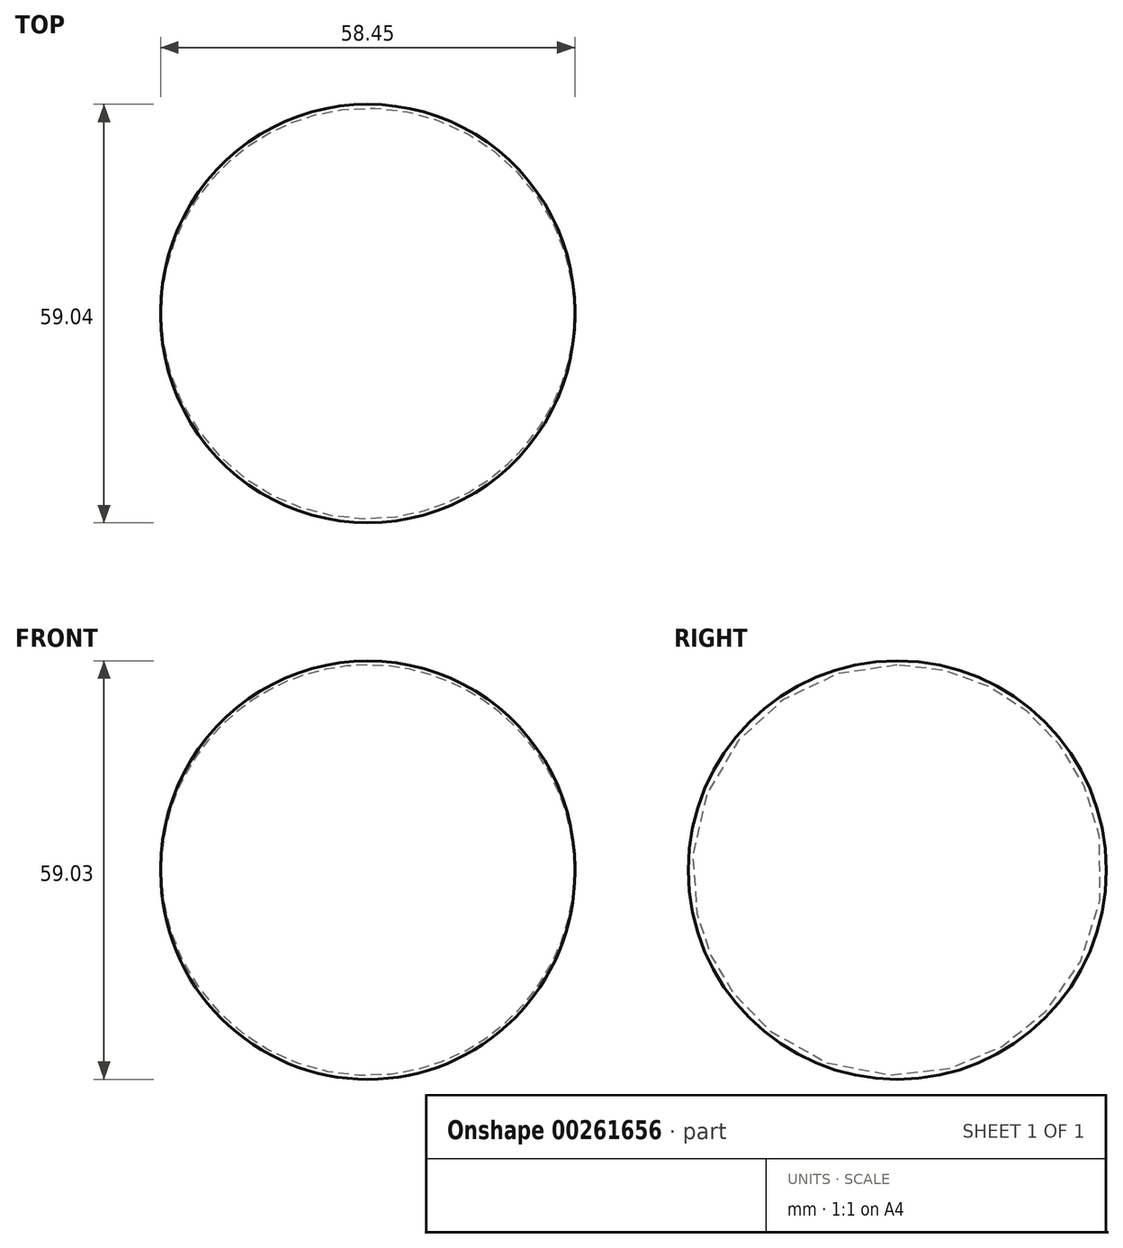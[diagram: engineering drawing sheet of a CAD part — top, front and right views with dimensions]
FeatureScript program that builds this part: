
annotation { "Feature Type Name" : "Feature", "Feature Type Description" : "" }
export const myFeature = defineFeature(function(context is Context, id is Id, definition is map)
    precondition{}
    {
        {
            var Q0;
            Q0=qCreatedBy(makeId("Front.planeOp"),FACE);
            var sketch = newSketch(context, id + "F0", { "sketchPlane" : qUnion([Q0])});
            skArc(sketch, "E0", {"start": v(20.11, 10.79) * mm, "mid": v(-9.11, 40.3) * mm, "end": v(-38.34, 10.79) * mm});
            skLineSegment(sketch, "E1", {"start": v(20.11, 10.79) * mm, "end": v(-38.34, 10.79) * mm});
            skSolve(sketch);
        }
        {
            var Q0;
            Q0=makeQuery(id+"F0.imprint","IMPRINT",FACE,{"disambiguationData":[TD([[makeQuery(id+"F0.imprint","IMPRINT",EDGE,{"derivedFrom":sQuery(id+"F0.wireOp",EDGE,"E0")}),1.0]])]});
            var Q1;
            Q1=sQuery(id+"F0.wireOp",EDGE,"E1");
            revolve(context, id + "F1", {"entities" : qUnion([Q0]), "axis" : qUnion([Q1]), "revolveType" : RevolveType.FULL});
        }
    });
